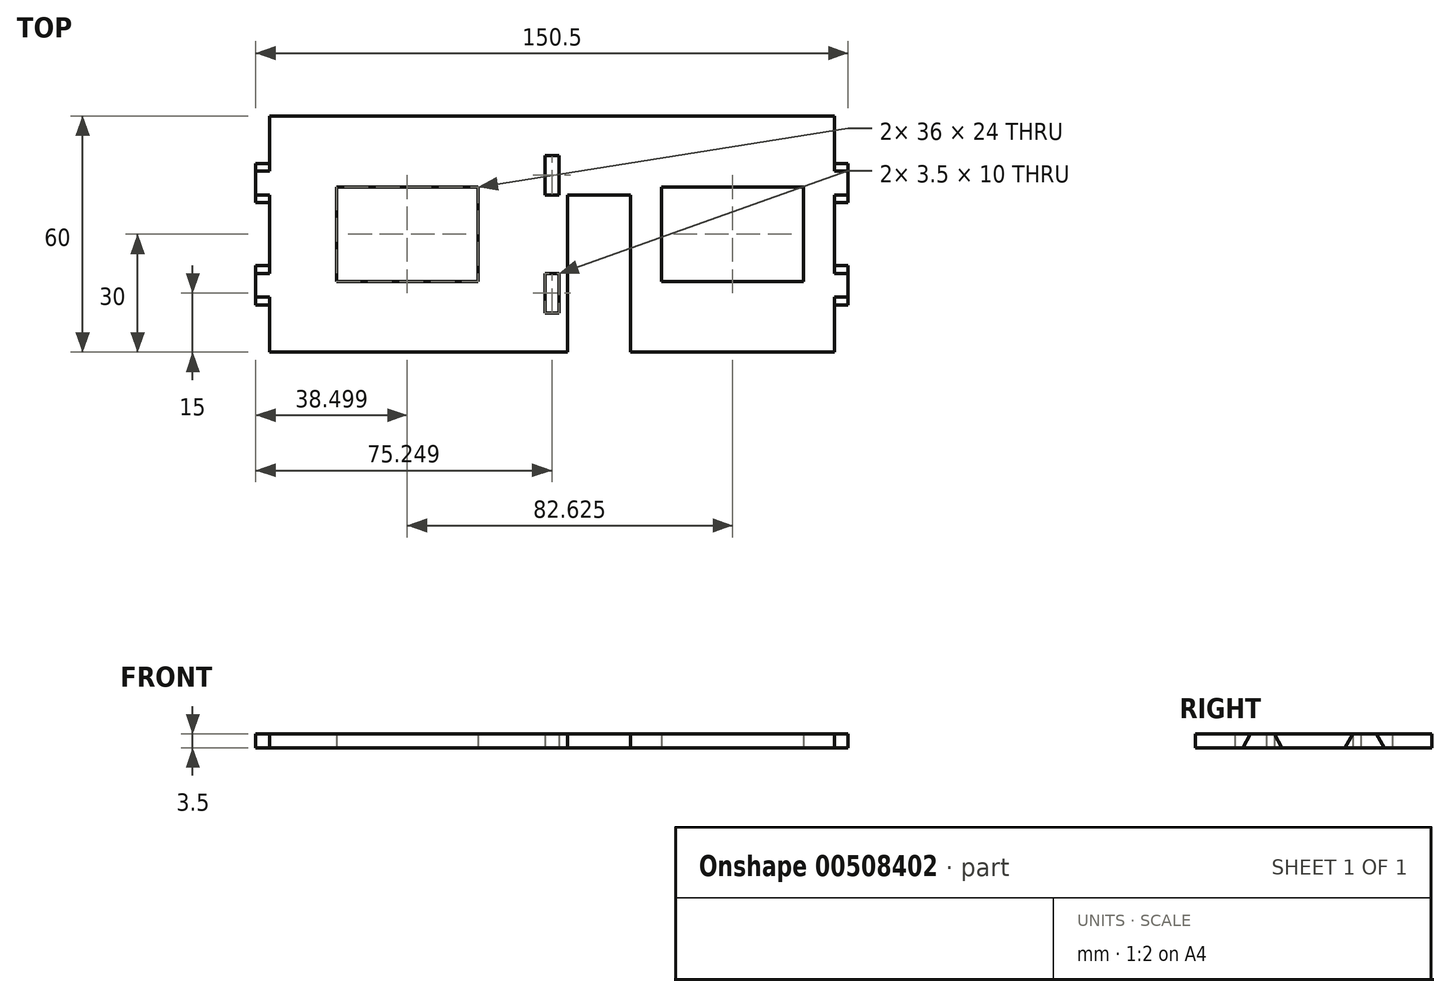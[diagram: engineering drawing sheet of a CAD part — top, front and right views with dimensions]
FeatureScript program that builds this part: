
annotation { "Feature Type Name" : "Feature", "Feature Type Description" : "" }
export const myFeature = defineFeature(function(context is Context, id is Id, definition is map)
    precondition{}
    {
        {
            var Q0;
            Q0=qCreatedBy(makeId("Top.planeOp"),FACE);
            var sketch = newSketch(context, id + "F0", { "sketchPlane" : qUnion([Q0])});
            skLineSegment(sketch, "E0", {"start": v(-55.53, 14.9) * mm, "end": v(-19.53, 14.9) * mm});
            skLineSegment(sketch, "E1", {"start": v(-19.53, 14.9) * mm, "end": v(-19.53, -9.1) * mm});
            skLineSegment(sketch, "E2", {"start": v(-19.53, -9.1) * mm, "end": v(-55.53, -9.1) * mm});
            skLineSegment(sketch, "E3", {"start": v(-55.53, -9.1) * mm, "end": v(-55.53, 14.9) * mm});
            skLineSegment(sketch, "E4", {"start": v(27.1, 14.9) * mm, "end": v(27.1, -9.1) * mm});
            skLineSegment(sketch, "E5", {"start": v(27.1, -9.1) * mm, "end": v(63.1, -9.1) * mm});
            skLineSegment(sketch, "E6", {"start": v(63.1, -9.1) * mm, "end": v(63.1, 14.9) * mm});
            skLineSegment(sketch, "E7", {"start": v(63.1, 14.9) * mm, "end": v(27.1, 14.9) * mm});
            skLineSegment(sketch, "E8", {"start": v(19.22, -27.1) * mm, "end": v(19.22, 12.9) * mm});
            skLineSegment(sketch, "E9", {"start": v(19.22, 12.9) * mm, "end": v(3.22, 12.9) * mm});
            skLineSegment(sketch, "E10", {"start": v(3.22, 12.9) * mm, "end": v(3.22, -27.1) * mm});
            skLineSegment(sketch, "E11", {"start": v(3.22, -27.1) * mm, "end": v(-76.03, -27.1) * mm});
            skLineSegment(sketch, "E12", {"start": v(-76.03, -27.1) * mm, "end": v(-76.03, 32.9) * mm});
            skLineSegment(sketch, "E13", {"start": v(-76.03, 32.9) * mm, "end": v(74.47, 32.9) * mm});
            skLineSegment(sketch, "E14", {"start": v(74.47, 32.9) * mm, "end": v(74.47, -27.1) * mm});
            skLineSegment(sketch, "E15", {"start": v(74.47, -27.1) * mm, "end": v(19.22, -27.1) * mm});
            skLineSegment(sketch, "E16", {"start": v(0.97, -17.1) * mm, "end": v(0.97, -7.1) * mm});
            skLineSegment(sketch, "E17", {"start": v(0.97, 12.9) * mm, "end": v(0.97, 22.9) * mm});
            skLineSegment(sketch, "E18", {"start": v(0.97, 12.9) * mm, "end": v(-2.53, 12.9) * mm});
            skLineSegment(sketch, "E19", {"start": v(-2.53, 12.9) * mm, "end": v(-2.53, 22.9) * mm});
            skLineSegment(sketch, "E20", {"start": v(-2.53, 22.9) * mm, "end": v(0.97, 22.9) * mm});
            skLineSegment(sketch, "E21", {"start": v(0.97, -17.1) * mm, "end": v(-2.53, -17.1) * mm});
            skLineSegment(sketch, "E22", {"start": v(-2.53, -17.1) * mm, "end": v(-2.53, -7.1) * mm});
            skLineSegment(sketch, "E23", {"start": v(-2.53, -7.1) * mm, "end": v(0.97, -7.1) * mm});
            skSolve(sketch);
        }
        {
            var Q0;
            Q0 = qSketchRegion(id + "F0", true);
            extrude(context, id + "F1", {"entities" : qUnion([Q0]), "depth" : 3.5 * mm, "offsetDistance" : 25 * mm});
        }
        {
            var Q0;
            Q0=makeQuery(id+"F1.opExtrude","SWEPT_FACE",FACE,{"disambiguationData":[OSD([sQuery(id+"F0.wireOp",EDGE,"E14")])]});
            var sketch = newSketch(context, id + "F2", { "sketchPlane" : qUnion([Q0])});
            skLineSegment(sketch, "E24", {"start": v(-27.1, 0) * mm, "end": v(-15.1, 0) * mm});
            skLineSegment(sketch, "E25", {"start": v(-15.1, 0) * mm, "end": v(-5.1, 0) * mm});
            skLineSegment(sketch, "E26", {"start": v(-5.1, 0) * mm, "end": v(10.9, 0) * mm});
            skLineSegment(sketch, "E27", {"start": v(10.9, 0) * mm, "end": v(20.9, 0) * mm});
            skLineSegment(sketch, "E28", {"start": v(20.9, 0) * mm, "end": v(32.9, 0) * mm});
            skLineSegment(sketch, "E29", {"start": v(32.9, 0) * mm, "end": v(32.9, 3.5) * mm});
            skLineSegment(sketch, "E30", {"start": v(32.9, 3.5) * mm, "end": v(18.9, 3.5) * mm});
            skLineSegment(sketch, "E31", {"start": v(18.9, 3.5) * mm, "end": v(12.9, 3.5) * mm});
            skLineSegment(sketch, "E32", {"start": v(12.9, 3.5) * mm, "end": v(-7.1, 3.5) * mm});
            skLineSegment(sketch, "E33", {"start": v(-7.1, 3.5) * mm, "end": v(-13.1, 3.5) * mm});
            skLineSegment(sketch, "E34", {"start": v(-13.1, 3.5) * mm, "end": v(-27.1, 3.5) * mm});
            skLineSegment(sketch, "E35", {"start": v(-27.1, 3.5) * mm, "end": v(-27.1, 0) * mm});
            skLineSegment(sketch, "E36", {"start": v(20.9, 0) * mm, "end": v(18.9, 3.5) * mm});
            skLineSegment(sketch, "E37", {"start": v(12.9, 3.5) * mm, "end": v(10.9, 0) * mm});
            skLineSegment(sketch, "E38", {"start": v(-5.1, 0) * mm, "end": v(-7.1, 3.5) * mm});
            skLineSegment(sketch, "E39", {"start": v(-13.1, 3.5) * mm, "end": v(-15.1, 0) * mm});
            skSolve(sketch);
        }
        {
            var Q0;
            Q0=makeQuery(id+"F2.imprint","IMPRINT",FACE,{"disambiguationData":[TD([[makeQuery(id+"F2.imprint","IMPRINT",EDGE,{"derivedFrom":sQuery(id+"F2.wireOp",EDGE,"E24")}),-1.0]])]});
            var Q1;
            Q1=makeQuery(id+"F2.imprint","IMPRINT",FACE,{"disambiguationData":[TD([[makeQuery(id+"F2.imprint","IMPRINT",EDGE,{"derivedFrom":sQuery(id+"F2.wireOp",EDGE,"E26")}),-1.0]])]});
            var Q2;
            Q2=makeQuery(id+"F2.imprint","IMPRINT",FACE,{"disambiguationData":[TD([[makeQuery(id+"F2.imprint","IMPRINT",EDGE,{"derivedFrom":sQuery(id+"F2.wireOp",EDGE,"E28")}),-1.0]])]});
            extrude(context, id + "F3", {"entities" : qUnion([Q0, Q1, Q2]), "operationType" : NewBodyOperationType.REMOVE, "oppositeDirection" : true, "depth" : 3.5 * mm, "offsetDistance" : 25 * mm});
        }
        {
            var Q0;
            Q0=makeQuery(id+"F1.opExtrude","SWEPT_FACE",FACE,{"disambiguationData":[OSD([sQuery(id+"F0.wireOp",EDGE,"E12")])]});
            var sketch = newSketch(context, id + "F4", { "sketchPlane" : qUnion([Q0])});
            skLineSegment(sketch, "E40", {"start": v(-32.9, 3.5) * mm, "end": v(-18.9, 3.5) * mm});
            skLineSegment(sketch, "E41", {"start": v(-18.9, 3.5) * mm, "end": v(-12.9, 3.5) * mm});
            skLineSegment(sketch, "E42", {"start": v(-12.9, 3.5) * mm, "end": v(7.1, 3.5) * mm});
            skLineSegment(sketch, "E43", {"start": v(7.1, 3.5) * mm, "end": v(13.1, 3.5) * mm});
            skLineSegment(sketch, "E44", {"start": v(13.1, 3.5) * mm, "end": v(27.1, 3.5) * mm});
            skLineSegment(sketch, "E45", {"start": v(27.1, 3.5) * mm, "end": v(27.1, 0) * mm});
            skLineSegment(sketch, "E46", {"start": v(27.1, 0) * mm, "end": v(15.1, 0) * mm});
            skLineSegment(sketch, "E47", {"start": v(15.1, 0) * mm, "end": v(5.1, 0) * mm});
            skLineSegment(sketch, "E48", {"start": v(5.1, 0) * mm, "end": v(-10.9, 0) * mm});
            skLineSegment(sketch, "E49", {"start": v(-10.9, 0) * mm, "end": v(-20.9, 0) * mm});
            skLineSegment(sketch, "E50", {"start": v(-20.9, 0) * mm, "end": v(-32.9, 0) * mm});
            skLineSegment(sketch, "E51", {"start": v(-32.9, 0) * mm, "end": v(-32.9, 3.5) * mm});
            skLineSegment(sketch, "E52", {"start": v(-18.9, 3.5) * mm, "end": v(-20.9, 0) * mm});
            skLineSegment(sketch, "E53", {"start": v(-12.9, 3.5) * mm, "end": v(-10.9, 0) * mm});
            skLineSegment(sketch, "E54", {"start": v(5.1, 0) * mm, "end": v(7.1, 3.5) * mm});
            skLineSegment(sketch, "E55", {"start": v(13.1, 3.5) * mm, "end": v(15.1, 0) * mm});
            skSolve(sketch);
        }
        {
            var Q0;
            Q0=makeQuery(id+"F4.imprint","IMPRINT",FACE,{"disambiguationData":[TD([[makeQuery(id+"F4.imprint","IMPRINT",EDGE,{"derivedFrom":sQuery(id+"F4.wireOp",EDGE,"E44")}),1.0]])]});
            var Q1;
            Q1=makeQuery(id+"F4.imprint","IMPRINT",FACE,{"disambiguationData":[TD([[makeQuery(id+"F4.imprint","IMPRINT",EDGE,{"derivedFrom":sQuery(id+"F4.wireOp",EDGE,"E42")}),1.0]])]});
            var Q2;
            Q2=makeQuery(id+"F4.imprint","IMPRINT",FACE,{"disambiguationData":[TD([[makeQuery(id+"F4.imprint","IMPRINT",EDGE,{"derivedFrom":sQuery(id+"F4.wireOp",EDGE,"E40")}),1.0]])]});
            extrude(context, id + "F5", {"entities" : qUnion([Q0, Q1, Q2]), "operationType" : NewBodyOperationType.REMOVE, "oppositeDirection" : true, "depth" : 3.5 * mm, "offsetDistance" : 25 * mm});
        }
    });
